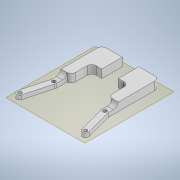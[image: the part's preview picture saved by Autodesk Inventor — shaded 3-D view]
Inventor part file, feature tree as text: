
AUTODESK INVENTOR PART (.ipt)
format: ipt  version: 2021 (Build 250183000, 183)  size: 232,960 bytes
history: native  units: mm
features: sketch x14, extrude x8, fillet x5, plane x3
ambient origin geometry x8: Origin, YZ Plane, XZ Plane, XY Plane, X Axis, Y Axis, Z Axis, Center Point
bodies: Solid1 (feature_tree)
feature tree (30):
  sketch  "Sketch1"  dims[d0=3.5mm d1=6.0mm]
  extrude  "Extrusion1"  Depth=6.0mm
  extrude  "Extrusion2"  Depth=4.75mm
  extrude  "Extrusion3"  Depth=6.0mm
  fillet  "Fillet1"  Radius=50.0mm
  fillet  "Fillet2"  Radius=6.0mm
  sketch  "Sketch5"  dims[d13=4.0mm d14=0.0mm d15=4.5mm]
  plane  "Work Plane2"
  fillet  "Fillet5"  Radius=4.0mm
  plane  "Work Plane1"
  sketch  "Sketch9"  dims[d16=4.5mm d34=4.5mm d35=27.0mm]
  sketch  "Sketch10"  dims[d36=6.0mm d37=3.5mm]
  extrude  "Extrusion7"  Depth=4.0mm TaperAngle=0.0deg
  plane  "Work Plane3"
  sketch  "Sketch13"  dims[d47=3.5mm]
  extrude  "Extrusion9"  Depth=4.5mm
  extrude  "Extrusion10"  Depth=4.5mm
  fillet  "Fillet6"  Radius=27.0mm
  extrude  "Extrusion11"  Depth=6.0mm
  extrude  "Extrusion12"  Depth=20.0mm
  sketch  "Sketch18"  dims[d54=40.0mm d55=4.0mm d56=0.0mm d57=40.0mm d58=4.0mm d59=0.0mm d60=4.5mm d61=20.0mm d62=10.0mm d63=0.0mm d64=20.0mm d65=10.0mm d66=0.0mm d67=4.5mm]
  fillet  "Fillet7"  Radius=20.0mm
  sketch  "Sketch2"  dims[d2=17.5mm d3=4.75mm]
  sketch  "Sketch3"  dims[d4=3.5mm d5=6.0mm d6=50.0mm d7=6.0mm d8=4.0mm d9=0.0mm]
  sketch  "Sketch4"  dims[d10=40.0mm d11=4.0mm d12=0.0mm]
  sketch  "Sketch11"  dims[d38=4.0mm d39=0.0mm d45=20.0mm d46=20.0mm]
  sketch  "Sketch14"  dims[d48=3.5mm]
  sketch  "Sketch15"  dims[d51=6.0mm]
  sketch  "Sketch16"  dims[d52=6.0mm]
  sketch  "Sketch17"  dims[d53=10.0mm]
